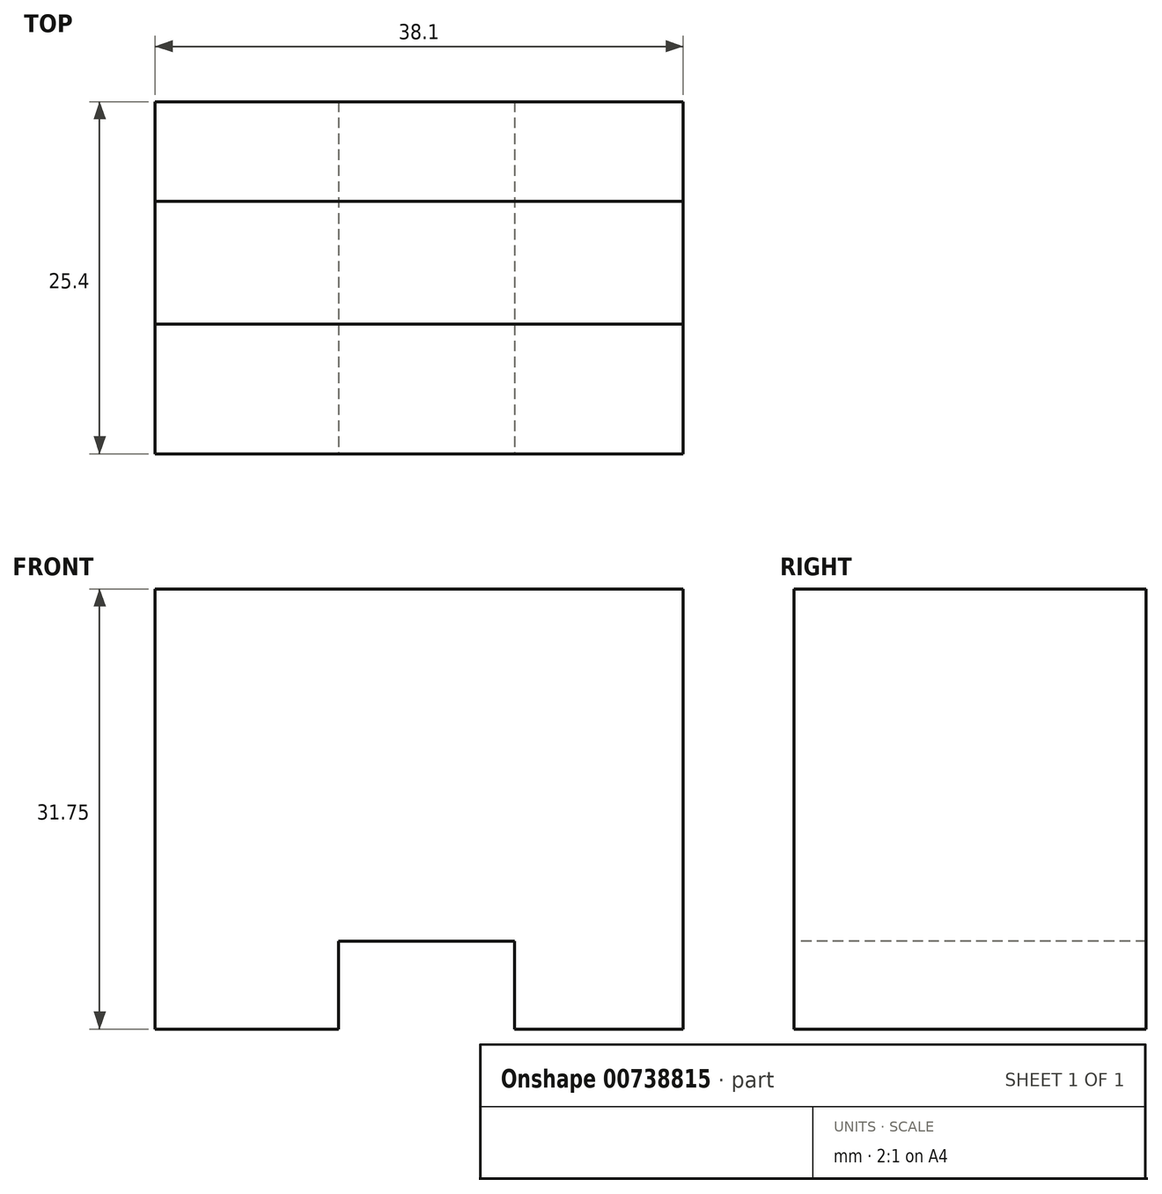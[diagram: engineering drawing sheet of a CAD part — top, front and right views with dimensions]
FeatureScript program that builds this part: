
annotation { "Feature Type Name" : "Feature", "Feature Type Description" : "" }
export const myFeature = defineFeature(function(context is Context, id is Id, definition is map)
    precondition{}
    {
        {
            var Q0;
            Q0=qCreatedBy(makeId("Front.planeOp"),FACE);
            var sketch = newSketch(context, id + "F0", { "sketchPlane" : qUnion([Q0])});
            skLineSegment(sketch, "E0", {"start": v(0, 0) * mm, "end": v(0, 31.75) * mm});
            skLineSegment(sketch, "E1", {"start": v(0, 31.75) * mm, "end": v(38.1, 31.75) * mm});
            skLineSegment(sketch, "E2", {"start": v(38.1, 31.75) * mm, "end": v(38.1, 0) * mm});
            skLineSegment(sketch, "E3", {"start": v(38.1, 0) * mm, "end": v(0, 0) * mm});
            skSolve(sketch);
        }
        {
            var Q0;
            Q0 = qSketchRegion(id + "F0", true);
            extrude(context, id + "F1", {"entities" : qUnion([Q0]), "depth" : 25.4 * mm, "offsetDistance" : 25.4 * mm});
        }
        {
            var Q0;
            Q0=makeQuery(id+"F1.opExtrude","CAP_FACE",FACE,{"disambiguationData":[OSD([sQuery(id+"F0.wireOp",EDGE,"E0"),sQuery(id+"F0.wireOp",EDGE,"E1"),sQuery(id+"F0.wireOp",EDGE,"E2"),sQuery(id+"F0.wireOp",EDGE,"E3")])],"isStart":false});
            var sketch = newSketch(context, id + "F2", { "sketchPlane" : qUnion([Q0])});
            skLineSegment(sketch, "E4", {"start": v(13.22, 0) * mm, "end": v(13.22, 6.35) * mm});
            skLineSegment(sketch, "E5", {"start": v(13.22, 6.35) * mm, "end": v(25.92, 6.35) * mm});
            skLineSegment(sketch, "E6", {"start": v(25.92, 6.35) * mm, "end": v(25.92, 0) * mm});
            skSolve(sketch);
        }
        {
            var Q0;
            {var subQ0=sQuery(id+"F2.wireOp",EDGE,"E4");Q0=makeQuery(id+"F2.imprint","IMPRINT",FACE,{"disambiguationData":[TD([[makeQuery(id+"F2.imprint","IMPRINT",EDGE,{"derivedFrom":subQ0}),-1.0]])]});}
            extrude(context, id + "F3", {"entities" : qUnion([Q0]), "operationType" : NewBodyOperationType.REMOVE, "endBound" : BoundingType.THROUGH_ALL, "oppositeDirection" : true, "depth" : 25.4 * mm, "offsetDistance" : 25.4 * mm});
        }
        {
            var Q0;
            Q0=makeQuery(id+"F1.opExtrude","SWEPT_FACE",FACE,{"disambiguationData":[OSD([sQuery(id+"F0.wireOp",EDGE,"E1")])]});
            var sketch = newSketch(context, id + "F4", { "sketchPlane" : qUnion([Q0])});
            skLineSegment(sketch, "E7", {"start": v(0, -7.18) * mm, "end": v(38.1, -7.18) * mm});
            skLineSegment(sketch, "E8", {"start": v(0, -16.06) * mm, "end": v(38.1, -16.06) * mm});
            skLineSegment(sketch, "E9", {"start": v(0, -7.18) * mm, "end": v(0, -16.06) * mm});
            skLineSegment(sketch, "E10", {"start": v(38.1, -7.18) * mm, "end": v(38.1, -16.06) * mm});
            skSolve(sketch);
        }
        {
            var Q0;
            Q0 = qSketchRegion(id + "F4", true);
            extrude(context, id + "F5", {"entities" : qUnion([Q0]), "operationType" : NewBodyOperationType.REMOVE, "oppositeDirection" : true, "depth" : 1 / 101.6 * mm, "offsetDistance" : 25.4 * mm});
        }
    });
